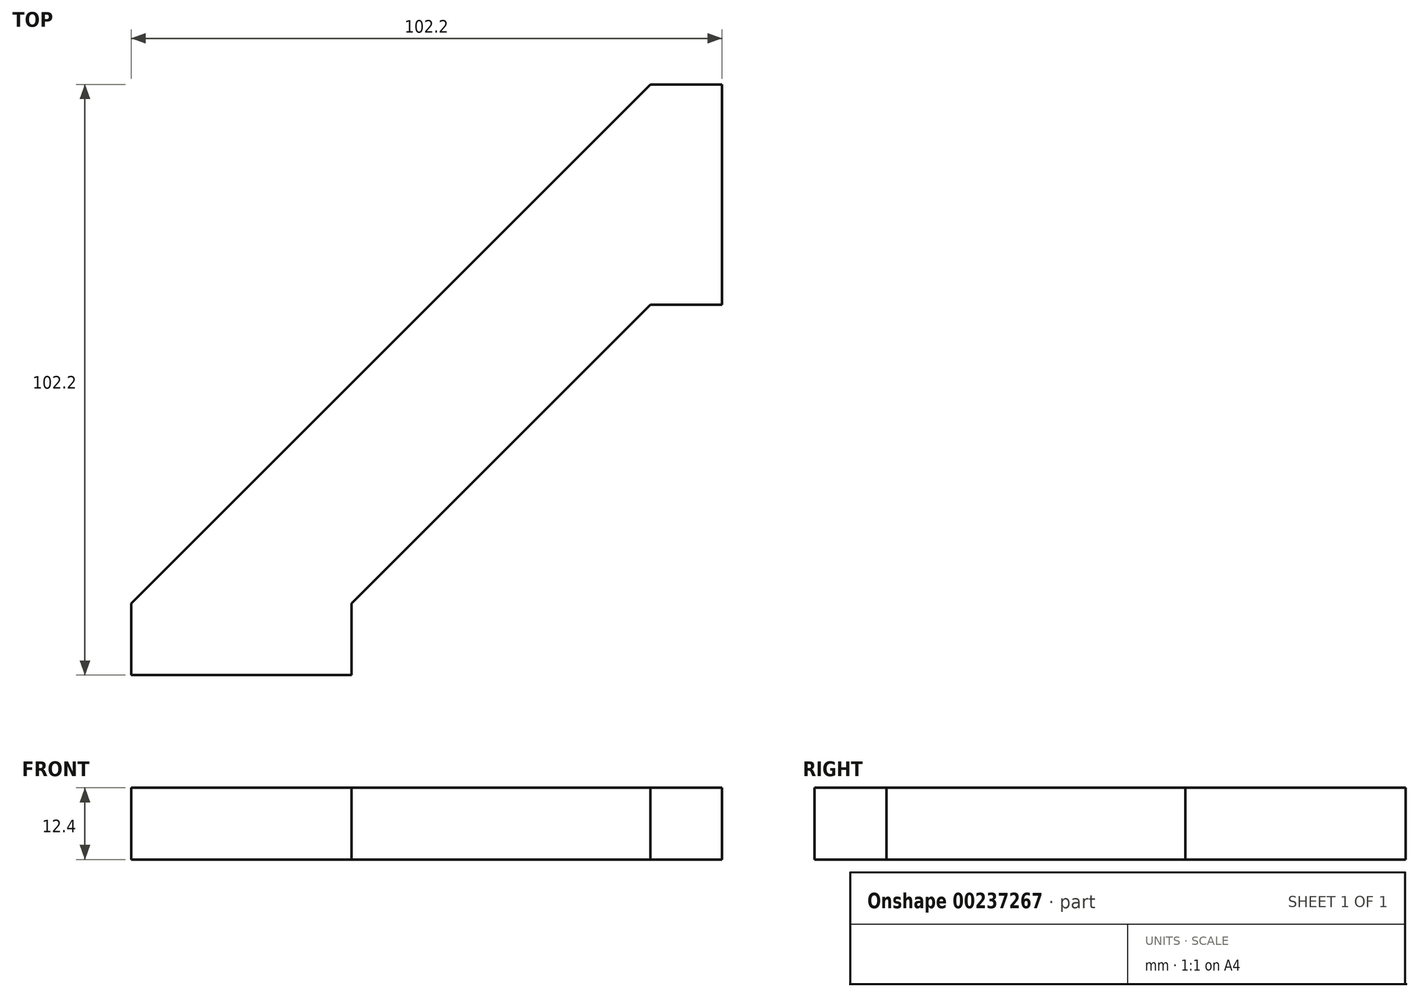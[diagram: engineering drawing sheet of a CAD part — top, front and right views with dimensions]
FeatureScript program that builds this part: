
annotation { "Feature Type Name" : "Feature", "Feature Type Description" : "" }
export const myFeature = defineFeature(function(context is Context, id is Id, definition is map)
    precondition{}
    {
        {
            var Q0;
            Q0=qCreatedBy(makeId("Top.planeOp"),FACE);
            var sketch = newSketch(context, id + "F0", { "sketchPlane" : qUnion([Q0])});
            skLineSegment(sketch, "E0", {"start": v(0, 0) * mm, "end": v(38.1, 0) * mm});
            skLineSegment(sketch, "E1", {"start": v(38.1, 0) * mm, "end": v(89.8, 51.7) * mm});
            skLineSegment(sketch, "E2", {"start": v(89.8, 51.7) * mm, "end": v(89.8, 89.8) * mm});
            skLineSegment(sketch, "E3", {"start": v(89.8, 89.8) * mm, "end": v(0, 0) * mm});
            skSolve(sketch);
        }
        {
            var Q0;
            Q0=makeQuery(id+"F0.imprint","IMPRINT",FACE,{"disambiguationData":[TD([[makeQuery(id+"F0.imprint","IMPRINT",EDGE,{"derivedFrom":sQuery(id+"F0.wireOp",EDGE,"E0")}),1.0]])]});
            extrude(context, id + "F1", {"entities" : qUnion([Q0]), "depth" : 12.4 * mm});
        }
        {
            var Q0;
            Q0=makeQuery(id+"F1.opExtrude","SWEPT_FACE",FACE,{"disambiguationData":[OSD([sQuery(id+"F0.wireOp",EDGE,"E2")])]});
            var sketch = newSketch(context, id + "F2", { "sketchPlane" : qUnion([Q0])});
            skSolve(sketch);
        }
        {
            var Q0;
            Q0 = qSketchRegion(id + "F2", true);
            var Q1;
            {var subQ0=sQuery(id+"F0.wireOp",EDGE,"E2");Q1=makeQuery(id+"F2.imprint","IMPRINT",FACE,{"disambiguationData":[TD([[makeQuery(id+"F2.imprint","IMPRINT",EDGE,{"derivedFrom":makeQuery(id+"F1.opExtrude","CAP_EDGE",EDGE,{"disambiguationData":[OSD([subQ0])],"isStart":true})}),1.0]])]});}
            extrude(context, id + "F3", {"entities" : qUnion([Q0, Q1]), "operationType" : NewBodyOperationType.ADD, "depth" : 12.4 * mm});
        }
        {
            var Q0;
            Q0=makeQuery(id+"F1.opExtrude","SWEPT_FACE",FACE,{"disambiguationData":[OSD([sQuery(id+"F0.wireOp",EDGE,"E0")])]});
            var sketch = newSketch(context, id + "F4", { "sketchPlane" : qUnion([Q0])});
            skLineSegment(sketch, "E4.bottom", {"start": v(0, 0) * mm, "end": v(38.1, 0) * mm});
            skLineSegment(sketch, "E4.top", {"start": v(0, 12.4) * mm, "end": v(38.1, 12.4) * mm});
            skLineSegment(sketch, "E4.left", {"start": v(0, 0) * mm, "end": v(0, 12.4) * mm});
            skLineSegment(sketch, "E4.right", {"start": v(38.1, 0) * mm, "end": v(38.1, 12.4) * mm});
            skSolve(sketch);
        }
        {
            var Q0;
            Q0 = qSketchRegion(id + "F4", true);
            extrude(context, id + "F5", {"entities" : qUnion([Q0]), "operationType" : NewBodyOperationType.ADD, "depth" : 12.4 * mm});
        }
    });
